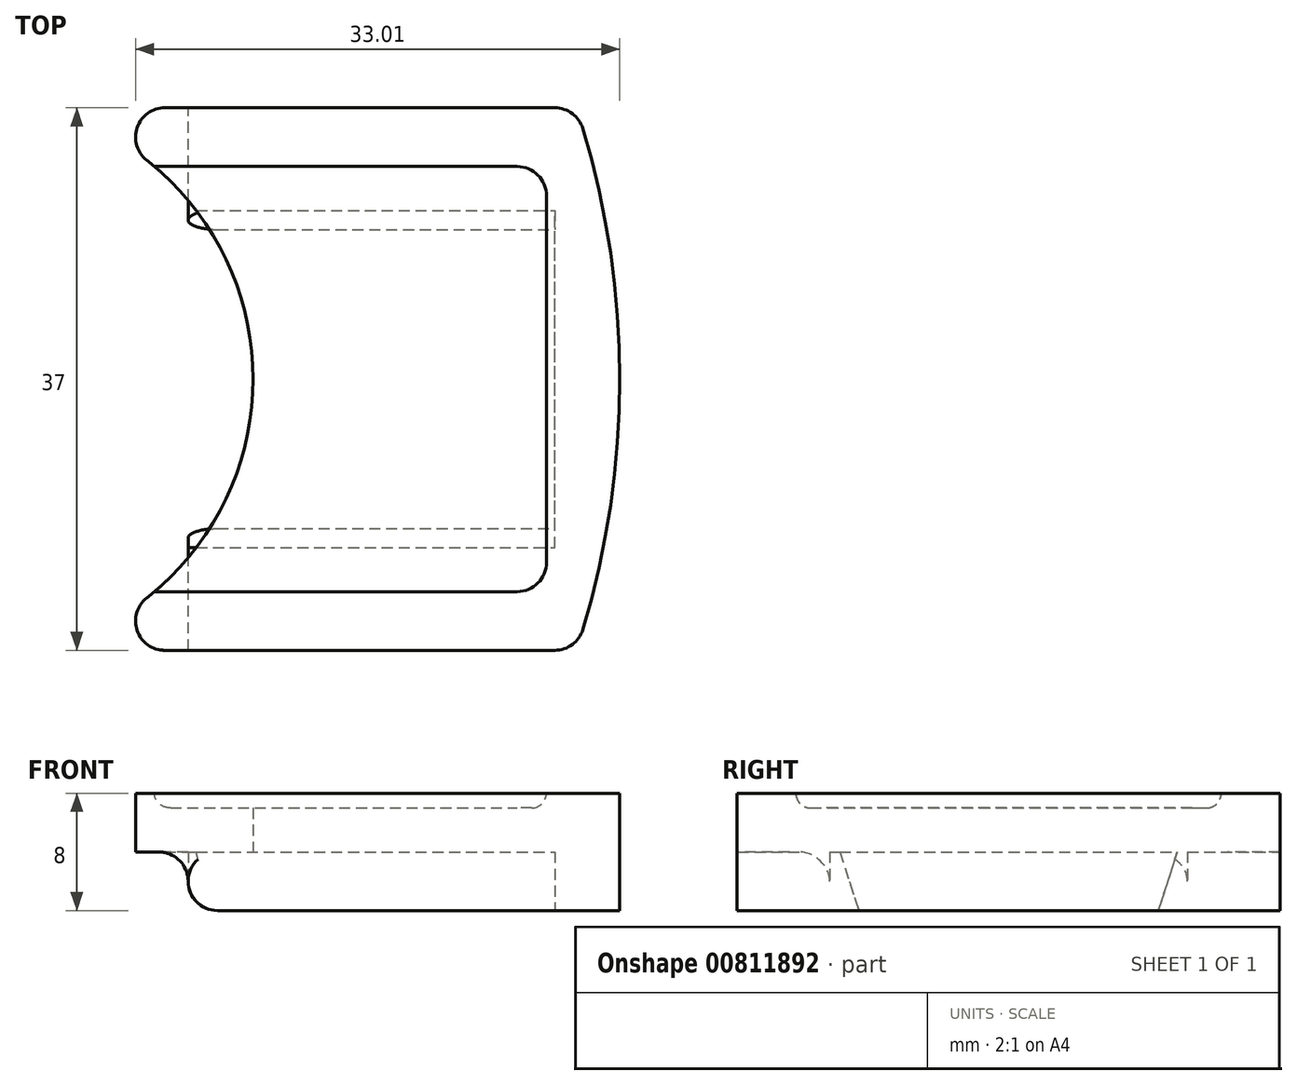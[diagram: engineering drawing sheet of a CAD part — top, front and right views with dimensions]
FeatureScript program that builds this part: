
annotation { "Feature Type Name" : "Feature", "Feature Type Description" : "" }
export const myFeature = defineFeature(function(context is Context, id is Id, definition is map)
    precondition{}
    {
        {
            var Q0;
            Q0=qCreatedBy(makeId("Top.planeOp"),FACE);
            var sketch = newSketch(context, id + "F0", { "sketchPlane" : qUnion([Q0])});
            skLineSegment(sketch, "E0", {"start": v(-19.77, 18.5) * mm, "end": v(6.81, 18.5) * mm});
            skArc(sketch, "E1", {"start": v(-13.76, 0) * mm, "mid": v(-15.67, 8.3) * mm, "end": v(-21, 14.93) * mm});
            skLineSegment(sketch, "E2", {"start": v(8.28, 18.5) * mm, "end": v(8.28, 18.5) * mm});
            skArc(sketch, "E3", {"start": v(11.24, 0) * mm, "mid": v(10.6, 8.63) * mm, "end": v(8.73, 17.08) * mm});
            skPoint(sketch, "E4.center.orphan", {"position": v(-51.25, 0) * mm});
            skArc(sketch, "E5.MirrorCS", {"start": v(-13.76, 0) * mm, "mid": v(-15.67, -8.3) * mm, "end": v(-21, -14.93) * mm});
            skLineSegment(sketch, "E6.MirrorCS", {"start": v(-19.77, -18.5) * mm, "end": v(6.81, -18.5) * mm});
            skArc(sketch, "E7.MirrorCS", {"start": v(11.24, 0) * mm, "mid": v(10.6, -8.63) * mm, "end": v(8.73, -17.08) * mm});
            skPoint(sketch, "E8.visualSharp", {"position": v(-28.43, 18.5) * mm});
            skArc(sketch, "E8.filletArc", {"start": v(-19.77, 18.5) * mm, "mid": v(-21.66, 17.15) * mm, "end": v(-21, 14.93) * mm});
            skPoint(sketch, "E9.visualSharp", {"position": v(-28.43, -18.5) * mm});
            skArc(sketch, "E9.filletArc", {"start": v(-21, -14.93) * mm, "mid": v(-21.66, -17.15) * mm, "end": v(-19.77, -18.5) * mm});
            skLineSegment(sketch, "E10", {"start": v(6.24, 12.5) * mm, "end": v(6.24, 0) * mm});
            skLineSegment(sketch, "E11", {"start": v(-20.48, 14.5) * mm, "end": v(4.24, 14.5) * mm});
            skPoint(sketch, "E12.visualSharp", {"position": v(6.24, 14.5) * mm});
            skArc(sketch, "E12.filletArc", {"start": v(6.24, 12.5) * mm, "mid": v(5.66, 13.91) * mm, "end": v(4.24, 14.5) * mm});
            skLineSegment(sketch, "E13.MirrorCS", {"start": v(-20.48, -14.5) * mm, "end": v(4.24, -14.5) * mm});
            skArc(sketch, "E14.MirrorCS", {"start": v(6.24, -12.5) * mm, "mid": v(5.66, -13.91) * mm, "end": v(4.24, -14.5) * mm});
            skLineSegment(sketch, "E15.MirrorCS", {"start": v(6.24, -12.5) * mm, "end": v(6.24, 0) * mm});
            skPoint(sketch, "E16.visualSharp", {"position": v(8.28, 18.5) * mm});
            skArc(sketch, "E16.filletArc", {"start": v(8.73, 17.08) * mm, "mid": v(8, 18.1) * mm, "end": v(6.81, 18.5) * mm});
            skArc(sketch, "E17.MirrorCS", {"start": v(8.73, -17.08) * mm, "mid": v(8, -18.1) * mm, "end": v(6.81, -18.5) * mm});
            skPoint(sketch, "E18.orphan", {"position": v(8.28, -18.5) * mm});
            skSolve(sketch);
        }
        {
            var Q0;
            Q0=makeQuery(id+"F0.imprint","IMPRINT",FACE,{"disambiguationData":[TD([[makeQuery(id+"F0.imprint","IMPRINT",EDGE,{"derivedFrom":sQuery(id+"F0.wireOp",EDGE,"E0")}),-1.0]])]});
            extrude(context, id + "F1", {"entities" : qUnion([Q0]), "depth" : 4 * mm, "offsetDistance" : 25 * mm});
        }
        {
            var Q0;
            Q0 = qSketchRegion(id + "F0", true);
            extrude(context, id + "F2", {"entities" : qUnion([Q0]), "operationType" : NewBodyOperationType.ADD, "depth" : 3 * mm, "offsetDistance" : 25 * mm});
        }
        {
            var Q0;
            Q0=makeQuery(id+"F2.boolean.opBoolean","INTERSECT",EDGE,{"derivedFrom":[makeQuery(id+"F1.opExtrude","SWEPT_FACE",FACE,{"disambiguationData":[OSD([sQuery(id+"F0.wireOp",EDGE,"E13.MirrorCS")])]}),makeQuery(id+"F2.opExtrude","CAP_FACE",FACE,{"disambiguationData":[OSD([sQuery(id+"F0.wireOp",EDGE,"E0"),sQuery(id+"F0.wireOp",EDGE,"E1"),sQuery(id+"F0.wireOp",EDGE,"E3"),sQuery(id+"F0.wireOp",EDGE,"E5.MirrorCS"),sQuery(id+"F0.wireOp",EDGE,"E6.MirrorCS"),sQuery(id+"F0.wireOp",EDGE,"E7.MirrorCS"),sQuery(id+"F0.wireOp",EDGE,"E8.filletArc"),sQuery(id+"F0.wireOp",EDGE,"E9.filletArc"),sQuery(id+"F0.wireOp",EDGE,"E16.filletArc"),sQuery(id+"F0.wireOp",EDGE,"E17.MirrorCS")])],"isStart":false})]});
            fillet(context, id + "F3", {"entities" : qUnion([Q0]), "radius" : 1 * mm, "tangentPropagation" : true, "allowEdgeOverflow" : false});
        }
        {
            var Q0;
            {var subQ0=sQuery(id+"F0.wireOp",EDGE,"E17.MirrorCS");var subQ1=sQuery(id+"F0.wireOp",EDGE,"E16.filletArc");var subQ2=sQuery(id+"F0.wireOp",EDGE,"E9.filletArc");var subQ3=sQuery(id+"F0.wireOp",EDGE,"E8.filletArc");var subQ4=sQuery(id+"F0.wireOp",EDGE,"E7.MirrorCS");var subQ5=sQuery(id+"F0.wireOp",EDGE,"E6.MirrorCS");var subQ6=sQuery(id+"F0.wireOp",EDGE,"E5.MirrorCS");var subQ7=sQuery(id+"F0.wireOp",EDGE,"E3");var subQ8=sQuery(id+"F0.wireOp",EDGE,"E1");var subQ9=sQuery(id+"F0.wireOp",EDGE,"E0");Q0=makeQuery(id+"F2.boolean.opBoolean","MERGE",FACE,{"derivedFrom":[makeQuery(id+"F1.opExtrude","CAP_FACE",FACE,{"disambiguationData":[OSD([subQ9,subQ8,subQ7,subQ6,subQ5,subQ4,subQ3,subQ2,sQuery(id+"F0.wireOp",EDGE,"E10"),sQuery(id+"F0.wireOp",EDGE,"E11"),sQuery(id+"F0.wireOp",EDGE,"E12.filletArc"),sQuery(id+"F0.wireOp",EDGE,"E13.MirrorCS"),sQuery(id+"F0.wireOp",EDGE,"E14.MirrorCS"),sQuery(id+"F0.wireOp",EDGE,"E15.MirrorCS"),subQ1,subQ0])],"isStart":true}),makeQuery(id+"F2.opExtrude","CAP_FACE",FACE,{"disambiguationData":[OSD([subQ9,subQ8,subQ7,subQ6,subQ5,subQ4,subQ3,subQ2,subQ1,subQ0])],"isStart":true})]});}
            var sketch = newSketch(context, id + "F4", { "sketchPlane" : qUnion([Q0])});
            skLineSegment(sketch, "E19", {"start": v(6.81, 18.5) * mm, "end": v(6.81, -18.5) * mm});
            skSolve(sketch);
        }
        {
            var Q0;
            Q0=makeQuery(id+"F4.imprint","IMPRINT",FACE,{"disambiguationData":[TD([[makeQuery(id+"F4.imprint","IMPRINT",EDGE,{"derivedFrom":sQuery(id+"F4.wireOp",EDGE,"E19")}),1.0]])]});
            extrude(context, id + "F5", {"entities" : qUnion([Q0]), "operationType" : NewBodyOperationType.ADD, "depth" : 4 * mm, "offsetDistance" : 25 * mm});
        }
        {
            var Q0;
            Q0=makeQuery(id+"F5.opExtrude","SWEPT_FACE",FACE,{"disambiguationData":[OSD([sQuery(id+"F4.wireOp",EDGE,"E19")])]});
            var sketch = newSketch(context, id + "F6", { "sketchPlane" : qUnion([Q0])});
            skLineSegment(sketch, "E20", {"start": v(-18.5, 0) * mm, "end": v(-11.5, 0) * mm});
            skLineSegment(sketch, "E21", {"start": v(-11.5, 0) * mm, "end": v(-10.2, -4) * mm});
            skLineSegment(sketch, "E22", {"start": v(-10.2, -4) * mm, "end": v(-18.5, -4) * mm});
            skLineSegment(sketch, "E23", {"start": v(-18.5, -4) * mm, "end": v(-18.5, 0) * mm});
            skLineSegment(sketch, "E24.MirrorCS", {"start": v(11.5, 0) * mm, "end": v(10.2, -4) * mm});
            skLineSegment(sketch, "E25.MirrorCS", {"start": v(10.2, -4) * mm, "end": v(18.5, -4) * mm});
            skLineSegment(sketch, "E26.MirrorCS", {"start": v(18.5, -4) * mm, "end": v(18.5, 0) * mm});
            skLineSegment(sketch, "E27.MirrorCS", {"start": v(18.5, 0) * mm, "end": v(11.5, 0) * mm});
            skSolve(sketch);
        }
        {
            var Q0;
            Q0=makeQuery(id+"F6.imprint","IMPRINT",FACE,{"disambiguationData":[TD([[makeQuery(id+"F6.imprint","IMPRINT",EDGE,{"derivedFrom":sQuery(id+"F6.wireOp",EDGE,"E20")}),1.0]])]});
            var Q1;
            Q1=makeQuery(id+"F6.imprint","IMPRINT",FACE,{"disambiguationData":[TD([[makeQuery(id+"F6.imprint","IMPRINT",EDGE,{"derivedFrom":sQuery(id+"F6.wireOp",EDGE,"E24.MirrorCS")}),1.0]])]});
            extrude(context, id + "F7", {"entities" : qUnion([Q0, Q1]), "operationType" : NewBodyOperationType.ADD, "depth" : 25 * mm, "offsetDistance" : 25 * mm});
        }
        {
            var Q0;
            {var subQ0=sQuery(id+"F0.wireOp",EDGE,"E17.MirrorCS");var subQ1=sQuery(id+"F0.wireOp",EDGE,"E16.filletArc");var subQ2=sQuery(id+"F0.wireOp",EDGE,"E9.filletArc");var subQ3=sQuery(id+"F0.wireOp",EDGE,"E8.filletArc");var subQ4=sQuery(id+"F0.wireOp",EDGE,"E7.MirrorCS");var subQ5=sQuery(id+"F0.wireOp",EDGE,"E6.MirrorCS");var subQ6=sQuery(id+"F0.wireOp",EDGE,"E5.MirrorCS");var subQ7=sQuery(id+"F0.wireOp",EDGE,"E3");var subQ8=sQuery(id+"F0.wireOp",EDGE,"E1");var subQ9=sQuery(id+"F0.wireOp",EDGE,"E0");var subQ10=sQuery(id+"F6.wireOp",EDGE,"E20");Q0=makeQuery(id+"F7.boolean.opBoolean","SPLIT",EDGE,{"disambiguationData":[topologyDisambiguationEdgeConnected([makeQuery(id+"F2.opExtrude","CAP_FACE",FACE,{"disambiguationData":[OSD([subQ9,subQ8,subQ7,subQ6,subQ5,subQ4,subQ3,subQ2,subQ1,subQ0])],"isStart":true})])],"derivedFrom":makeQuery(id+"F7.opExtrude","CAP_EDGE",EDGE,{"disambiguationData":[OSD([subQ10])],"isStart":false})});}
            var Q1;
            {var subQ0=sQuery(id+"F0.wireOp",EDGE,"E17.MirrorCS");var subQ1=sQuery(id+"F0.wireOp",EDGE,"E16.filletArc");var subQ2=sQuery(id+"F0.wireOp",EDGE,"E9.filletArc");var subQ3=sQuery(id+"F0.wireOp",EDGE,"E8.filletArc");var subQ4=sQuery(id+"F0.wireOp",EDGE,"E7.MirrorCS");var subQ5=sQuery(id+"F0.wireOp",EDGE,"E6.MirrorCS");var subQ6=sQuery(id+"F0.wireOp",EDGE,"E5.MirrorCS");var subQ7=sQuery(id+"F0.wireOp",EDGE,"E3");var subQ8=sQuery(id+"F0.wireOp",EDGE,"E1");var subQ9=sQuery(id+"F0.wireOp",EDGE,"E0");var subQ10=sQuery(id+"F6.wireOp",EDGE,"E27.MirrorCS");Q1=makeQuery(id+"F7.boolean.opBoolean","SPLIT",EDGE,{"disambiguationData":[topologyDisambiguationEdgeConnected([makeQuery(id+"F2.opExtrude","CAP_FACE",FACE,{"disambiguationData":[OSD([subQ9,subQ8,subQ7,subQ6,subQ5,subQ4,subQ3,subQ2,subQ1,subQ0])],"isStart":true})])],"derivedFrom":makeQuery(id+"F7.opExtrude","CAP_EDGE",EDGE,{"disambiguationData":[OSD([subQ10])],"isStart":false})});}
            var Q2;
            Q2=makeQuery(id+"F7.opExtrude","CAP_EDGE",EDGE,{"disambiguationData":[OSD([sQuery(id+"F6.wireOp",EDGE,"E22")])],"isStart":false});
            var Q3;
            Q3=makeQuery(id+"F7.opExtrude","CAP_EDGE",EDGE,{"disambiguationData":[OSD([sQuery(id+"F6.wireOp",EDGE,"E25.MirrorCS")])],"isStart":false});
            fillet(context, id + "F8", {"entities" : qUnion([Q0, Q1, Q2, Q3]), "radius" : 2 * mm, "tangentPropagation" : true, "allowEdgeOverflow" : false});
        }
    });
